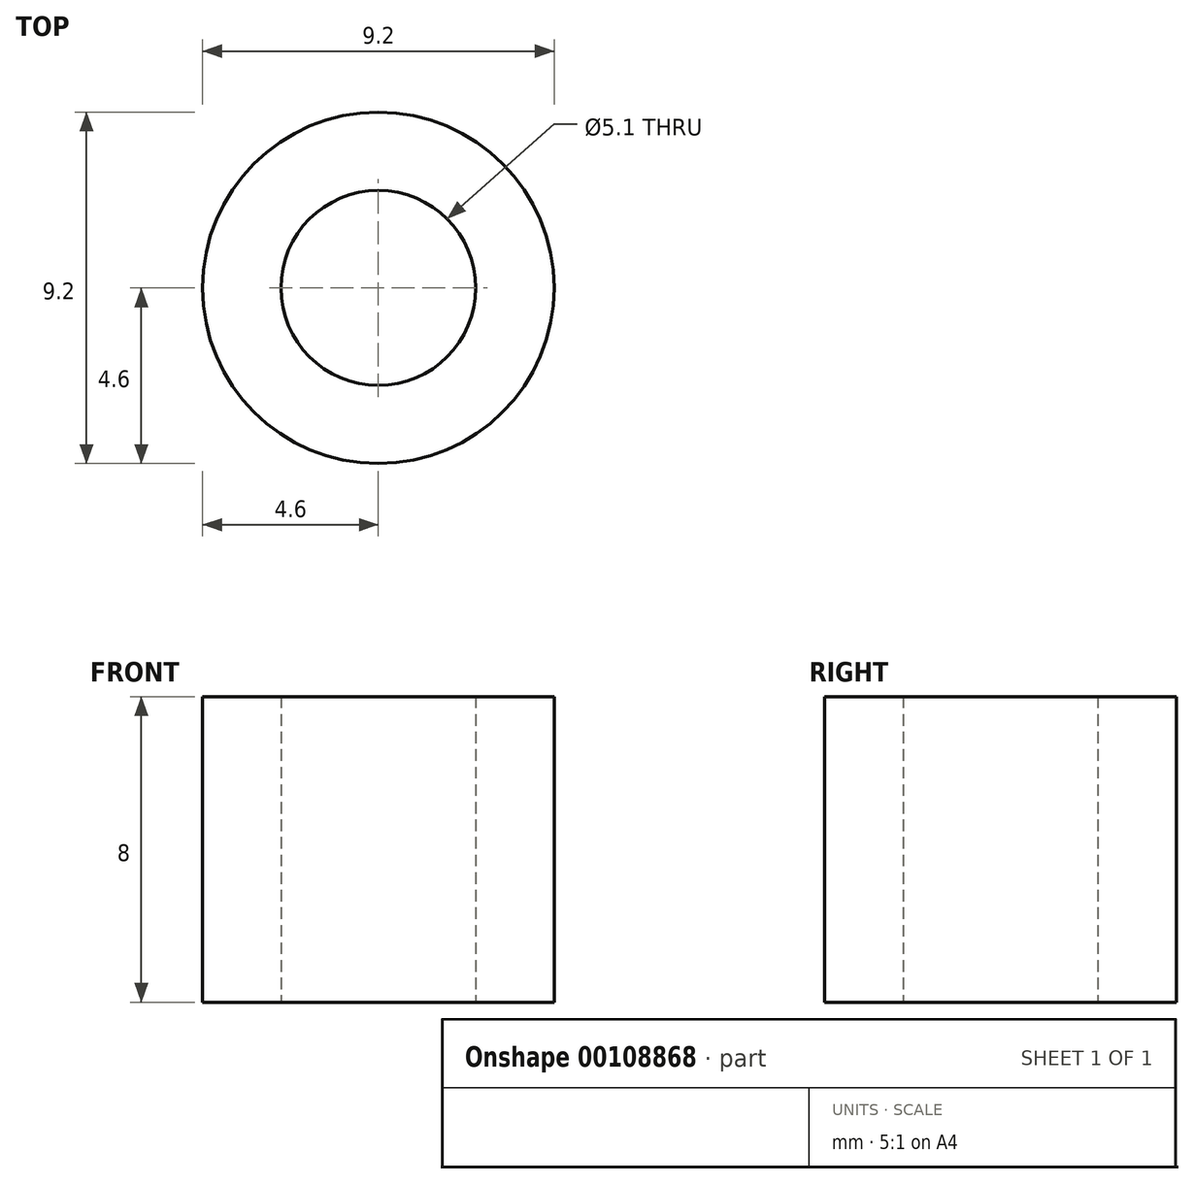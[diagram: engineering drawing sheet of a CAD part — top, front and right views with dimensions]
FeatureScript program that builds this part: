
annotation { "Feature Type Name" : "Feature", "Feature Type Description" : "" }
export const myFeature = defineFeature(function(context is Context, id is Id, definition is map)
    precondition{}
    {
        {
            var Q0;
            Q0=qCreatedBy(makeId("Top.planeOp"),FACE);
            var sketch = newSketch(context, id + "F0", { "sketchPlane" : qUnion([Q0])});
            skLineSegment(sketch, "E0", {"start": v(-17.27, 0) * mm, "end": v(19.18, 0) * mm, "construction": true});
            skLineSegment(sketch, "E1", {"start": v(0, -15.58) * mm, "end": v(0, -13.79) * mm, "construction": true});
            skLineSegment(sketch, "E2", {"start": v(0, 9.98) * mm, "end": v(0, -10.83) * mm, "construction": true});
            skCircle(sketch, "E3", {"center": v(0, 0) * mm, "radius": 2.55 * mm});
            skCircle(sketch, "E4", {"center": v(0, 0) * mm, "radius": 4.6 * mm});
            skSolve(sketch);
        }
        {
            var Q0;
            Q0=makeQuery(id+"F0.imprint","IMPRINT",FACE,{"disambiguationData":[TD([[makeQuery(id+"F0.imprint","IMPRINT",EDGE,{"derivedFrom":sQuery(id+"F0.wireOp",EDGE,"E3")}),-1.0]])]});
            extrude(context, id + "F1", {"entities" : qUnion([Q0]), "depth" : 8 * mm});
        }
    });
